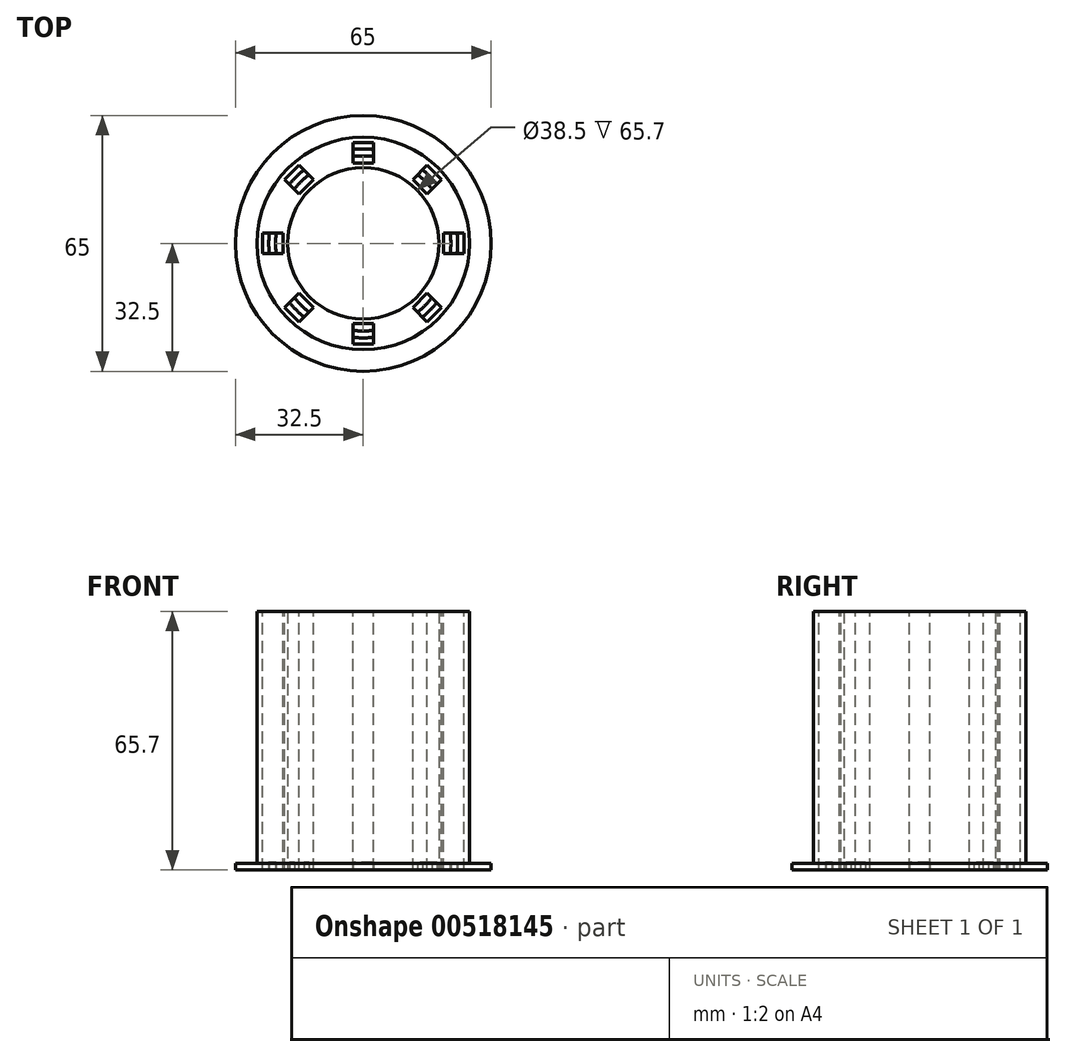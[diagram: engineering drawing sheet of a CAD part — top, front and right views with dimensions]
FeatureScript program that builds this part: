
annotation { "Feature Type Name" : "Feature", "Feature Type Description" : "" }
export const myFeature = defineFeature(function(context is Context, id is Id, definition is map)
    precondition{}
    {
        {
            var Q0;
            Q0=qCreatedBy(makeId("Top.planeOp"),FACE);
            var sketch = newSketch(context, id + "F0", { "sketchPlane" : qUnion([Q0])});
            skCircle(sketch, "E0", {"center": v(0, 0) * mm, "radius": 27 * mm});
            skCircle(sketch, "E1", {"center": v(0, 0) * mm, "radius": 19.25 * mm});
            skSolve(sketch);
        }
        {
            var Q0;
            Q0 = qSketchRegion(id + "F0", true);
            extrude(context, id + "F1", {"entities" : qUnion([Q0]), "depth" : 64 * mm, "offsetDistance" : 25 * mm});
        }
        {
            var Q0;
            Q0=makeQuery(id+"F1.opExtrude","CAP_FACE",FACE,{"disambiguationData":[OSD([sQuery(id+"F0.wireOp",EDGE,"E0"),sQuery(id+"F0.wireOp",EDGE,"E1")])],"isStart":true});
            var sketch = newSketch(context, id + "F2", { "sketchPlane" : qUnion([Q0])});
            skCircle(sketch, "E2", {"center": v(0, 0) * mm, "radius": 32.5 * mm});
            skCircle(sketch, "E3", {"center": v(0, 0) * mm, "radius": 19.25 * mm});
            skSolve(sketch);
        }
        {
            var Q0;
            Q0 = qSketchRegion(id + "F2", true);
            extrude(context, id + "F3", {"entities" : qUnion([Q0]), "operationType" : NewBodyOperationType.ADD, "depth" : 1.7 * mm, "offsetDistance" : 25 * mm});
        }
        {
            var Q0;
            Q0=makeQuery(id+"F1.opExtrude","CAP_FACE",FACE,{"disambiguationData":[OSD([sQuery(id+"F0.wireOp",EDGE,"E0"),sQuery(id+"F0.wireOp",EDGE,"E1")])],"isStart":false});
            var sketch = newSketch(context, id + "F4", { "sketchPlane" : qUnion([Q0])});
            skLineSegment(sketch, "E4", {"start": v(0, 0) * mm, "end": v(0, -23) * mm, "construction": true});
            skLineSegment(sketch, "E5.bottom", {"start": v(-2.6, -20.4) * mm, "end": v(2.6, -20.4) * mm});
            skLineSegment(sketch, "E5.top", {"start": v(-2.6, -25.6) * mm, "end": v(2.6, -25.6) * mm});
            skLineSegment(sketch, "E5.left", {"start": v(-2.6, -20.4) * mm, "end": v(-2.6, -25.6) * mm});
            skLineSegment(sketch, "E5.right", {"start": v(2.6, -20.4) * mm, "end": v(2.6, -25.6) * mm});
            skPoint(sketch, "E5.middle", {"position": v(0, -23) * mm});
            skLineSegment(sketch, "E6.1.0", {"start": v(12.59, -16.26) * mm, "end": v(16.26, -19.94) * mm});
            skLineSegment(sketch, "E6.1.1", {"start": v(12.59, -16.26) * mm, "end": v(16.26, -12.59) * mm});
            skLineSegment(sketch, "E6.1.2", {"start": v(16.26, -19.94) * mm, "end": v(19.94, -16.26) * mm});
            skLineSegment(sketch, "E6.1.3", {"start": v(16.26, -12.59) * mm, "end": v(19.94, -16.26) * mm});
            skLineSegment(sketch, "E6.2.0", {"start": v(20.4, -2.6) * mm, "end": v(25.6, -2.6) * mm});
            skLineSegment(sketch, "E6.2.1", {"start": v(20.4, -2.6) * mm, "end": v(20.4, 2.6) * mm});
            skLineSegment(sketch, "E6.2.2", {"start": v(25.6, -2.6) * mm, "end": v(25.6, 2.6) * mm});
            skLineSegment(sketch, "E6.2.3", {"start": v(20.4, 2.6) * mm, "end": v(25.6, 2.6) * mm});
            skLineSegment(sketch, "E6.3.0", {"start": v(16.26, 12.59) * mm, "end": v(19.94, 16.26) * mm});
            skLineSegment(sketch, "E6.3.1", {"start": v(16.26, 12.59) * mm, "end": v(12.59, 16.26) * mm});
            skLineSegment(sketch, "E6.3.2", {"start": v(19.94, 16.26) * mm, "end": v(16.26, 19.94) * mm});
            skLineSegment(sketch, "E6.3.3", {"start": v(12.59, 16.26) * mm, "end": v(16.26, 19.94) * mm});
            skLineSegment(sketch, "E6.4.0", {"start": v(2.6, 20.4) * mm, "end": v(2.6, 25.6) * mm});
            skLineSegment(sketch, "E6.4.1", {"start": v(2.6, 20.4) * mm, "end": v(-2.6, 20.4) * mm});
            skLineSegment(sketch, "E6.4.2", {"start": v(2.6, 25.6) * mm, "end": v(-2.6, 25.6) * mm});
            skLineSegment(sketch, "E6.4.3", {"start": v(-2.6, 20.4) * mm, "end": v(-2.6, 25.6) * mm});
            skLineSegment(sketch, "E6.5.0", {"start": v(-12.59, 16.26) * mm, "end": v(-16.26, 19.94) * mm});
            skLineSegment(sketch, "E6.5.1", {"start": v(-12.59, 16.26) * mm, "end": v(-16.26, 12.59) * mm});
            skLineSegment(sketch, "E6.5.2", {"start": v(-16.26, 19.94) * mm, "end": v(-19.94, 16.26) * mm});
            skLineSegment(sketch, "E6.5.3", {"start": v(-16.26, 12.59) * mm, "end": v(-19.94, 16.26) * mm});
            skLineSegment(sketch, "E6.6.0", {"start": v(-20.4, 2.6) * mm, "end": v(-25.6, 2.6) * mm});
            skLineSegment(sketch, "E6.6.1", {"start": v(-20.4, 2.6) * mm, "end": v(-20.4, -2.6) * mm});
            skLineSegment(sketch, "E6.6.2", {"start": v(-25.6, 2.6) * mm, "end": v(-25.6, -2.6) * mm});
            skLineSegment(sketch, "E6.6.3", {"start": v(-20.4, -2.6) * mm, "end": v(-25.6, -2.6) * mm});
            skLineSegment(sketch, "E6.7.0", {"start": v(-16.26, -12.59) * mm, "end": v(-19.94, -16.26) * mm});
            skLineSegment(sketch, "E6.7.1", {"start": v(-16.26, -12.59) * mm, "end": v(-12.59, -16.26) * mm});
            skLineSegment(sketch, "E6.7.2", {"start": v(-19.94, -16.26) * mm, "end": v(-16.26, -19.94) * mm});
            skLineSegment(sketch, "E6.7.3", {"start": v(-12.59, -16.26) * mm, "end": v(-16.26, -19.94) * mm});
            skPoint(sketch, "E6.center", {"position": v(0, 0) * mm});
            skSolve(sketch);
        }
        {
            var Q0;
            Q0 = qSketchRegion(id + "F4", true);
            extrude(context, id + "F5", {"entities" : qUnion([Q0]), "operationType" : NewBodyOperationType.REMOVE, "endBound" : BoundingType.THROUGH_ALL, "oppositeDirection" : true, "depth" : 62 * mm, "offsetDistance" : 25 * mm});
        }
        {
            var Q0;
            Q0=makeQuery(id+"F3.opExtrude","CAP_FACE",FACE,{"disambiguationData":[OSD([sQuery(id+"F2.wireOp",EDGE,"E2"),sQuery(id+"F2.wireOp",EDGE,"E3")])],"isStart":false});
            var sketch = newSketch(context, id + "F6", { "sketchPlane" : qUnion([Q0])});
            skCircle(sketch, "E7", {"center": v(0, 0) * mm, "radius": 24 * mm});
            skCircle(sketch, "E8", {"center": v(0, 0) * mm, "radius": 22.25 * mm});
            skSolve(sketch);
        }
        {
            var Q0;
            Q0 = qSketchRegion(id + "F6", true);
            extrude(context, id + "F7", {"entities" : qUnion([Q0]), "operationType" : NewBodyOperationType.ADD, "oppositeDirection" : true, "depth" : 2 * mm, "offsetDistance" : 25 * mm});
        }
    });
